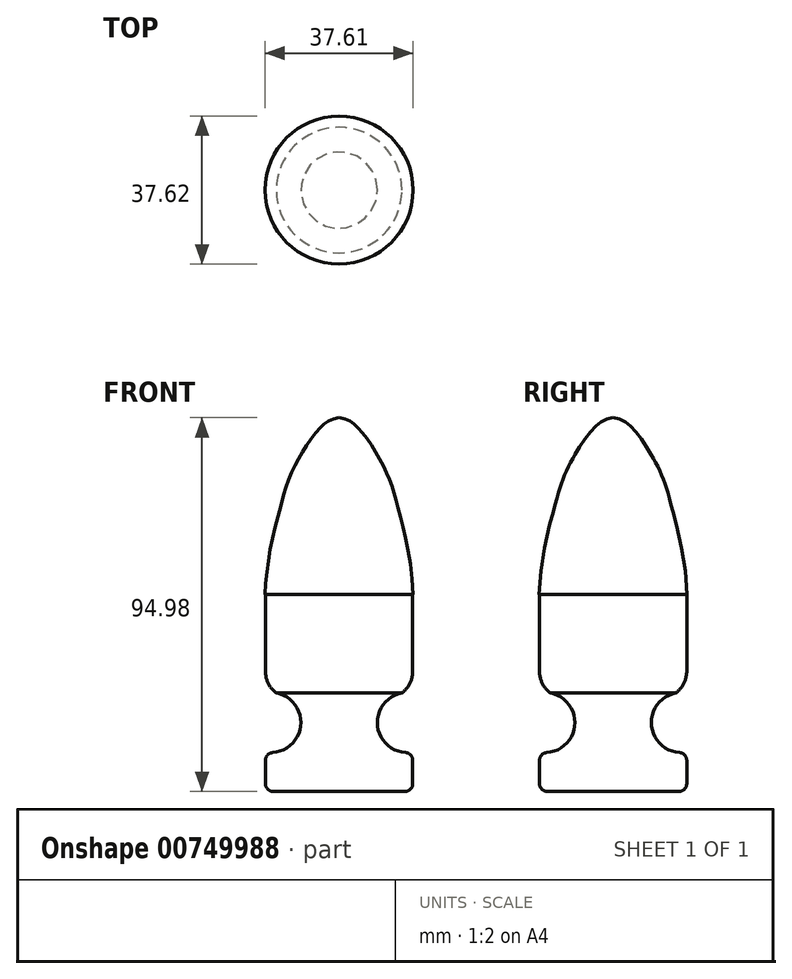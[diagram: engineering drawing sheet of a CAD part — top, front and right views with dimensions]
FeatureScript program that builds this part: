
annotation { "Feature Type Name" : "Feature", "Feature Type Description" : "" }
export const myFeature = defineFeature(function(context is Context, id is Id, definition is map)
    precondition{}
    {
        {
            var Q0;
            Q0=qCreatedBy(makeId("Front.planeOp"),FACE);
            var sketch = newSketch(context, id + "F0", { "sketchPlane" : qUnion([Q0])});
            skLineSegment(sketch, "E0", {"start": v(15.25, 0) * mm, "end": v(18, 0) * mm, "construction": true});
            skLineSegment(sketch, "E1", {"start": v(-0.7, 69.98) * mm, "end": v(-15.52, 72.3) * mm, "construction": true});
            skPoint(sketch, "E2", {"position": v(18.1, 25) * mm});
            skFitSpline(sketch, "E3", {"points": [v(18.1, 25) * mm, v(14.14, 47.46) * mm, v(11.85, 54.85) * mm, v(7.6, 62.87) * mm, v(3.17, 68.33) * mm, v(-0.7, 69.98) * mm], "startDerivative": vector(-4.12, 96.85) * mm, "endDerivative": vector(-40.5, 6.33) * mm});
            skLineSegment(sketch, "E4", {"start": v(18.1, 25) * mm, "end": v(18, 0) * mm, "construction": true});
            skLineSegment(sketch, "E5", {"start": v(18, 0) * mm, "end": v(18, -15) * mm, "construction": true});
            skLineSegment(sketch, "E6.top", {"start": v(18, -25) * mm, "end": v(-0.7, -25) * mm});
            skLineSegment(sketch, "E6.left", {"start": v(18, -15) * mm, "end": v(18, -25) * mm});
            skLineSegment(sketch, "E6.right", {"start": v(-0.7, -15) * mm, "end": v(-0.7, -25) * mm, "construction": true});
            skLineSegment(sketch, "E7", {"start": v(-0.7, 69.98) * mm, "end": v(-0.7, 25.08) * mm});
            skPoint(sketch, "E8", {"position": v(18, -7.5) * mm});
            skLineSegment(sketch, "E9", {"start": v(18, -7.5) * mm, "end": v(9, -7.5) * mm, "construction": true});
            skArc(sketch, "E10", {"start": v(18, 0) * mm, "mid": v(9, -7.5) * mm, "end": v(18, -15) * mm});
            skLineSegment(sketch, "E11", {"start": v(18.1, 25) * mm, "end": v(-0.7, 25.08) * mm});
            skPoint(sketch, "E12", {"position": v(-0.7, 0) * mm});
            skPoint(sketch, "E13", {"position": v(-5.04, 35.14) * mm});
            skLineSegment(sketch, "E14.trimOffspring", {"start": v(-0.7, 0) * mm, "end": v(-0.7, -25) * mm});
            skLineSegment(sketch, "E15", {"start": v(18, 0) * mm, "end": v(-0.7, 0) * mm, "construction": true});
            skLineSegment(sketch, "E16.bottom", {"start": v(-0.7, 25.08) * mm, "end": v(18, 25.08) * mm});
            skLineSegment(sketch, "E16.top", {"start": v(-0.7, 0) * mm, "end": v(18, 0) * mm});
            skLineSegment(sketch, "E16.left", {"start": v(-0.7, 25.08) * mm, "end": v(-0.7, 0) * mm});
            skLineSegment(sketch, "E16.right", {"start": v(18, 25.08) * mm, "end": v(18, 0) * mm});
            skSolve(sketch);
        }
        {
            var Q0;
            Q0 = qSketchRegion(id + "F0", true);
            var Q1;
            Q1=sQuery(id+"F0.wireOp",EDGE,"E7");
            revolve(context, id + "F1", {"surfaceOperationType" : NewSurfaceOperationType.NEW, "entities" : qUnion([Q0]), "axis" : qUnion([Q1]), "revolveType" : RevolveType.FULL});
        }
        {
            var Q0;
            Q0=makeQuery(id+"F1.opRevolve","SWEPT_EDGE",EDGE,{"disambiguationData":[OSD([sQuery(id+"F0.wireOp",EDGE,"E6.left"),sQuery(id+"F0.wireOp",EDGE,"E10")])]});
            var Q1;
            Q1=makeQuery(id+"F1.opRevolve","SWEPT_EDGE",EDGE,{"disambiguationData":[OSD([sQuery(id+"F0.wireOp",EDGE,"E6.top"),sQuery(id+"F0.wireOp",EDGE,"E6.left")])]});
            fillet(context, id + "F2", {"entities" : qUnion([Q0, Q1]), "tangentPropagation" : true, "radius" : 2 * mm, "defaultsChanged" : true, "vertexSettings" : [], "allowEdgeOverflow" : false});
        }
        {
            var Q0;
            Q0=makeQuery(id+"F1.opRevolve","SWEPT_EDGE",EDGE,{"disambiguationData":[OSD([sQuery(id+"F0.wireOp",EDGE,"E10"),sQuery(id+"F0.wireOp",EDGE,"E16.top"),sQuery(id+"F0.wireOp",EDGE,"E16.right")])]});
            fillet(context, id + "F3", {"entities" : qUnion([Q0]), "tangentPropagation" : true, "radius" : 7 * mm, "defaultsChanged" : true, "vertexSettings" : [], "allowEdgeOverflow" : false});
        }
    });
